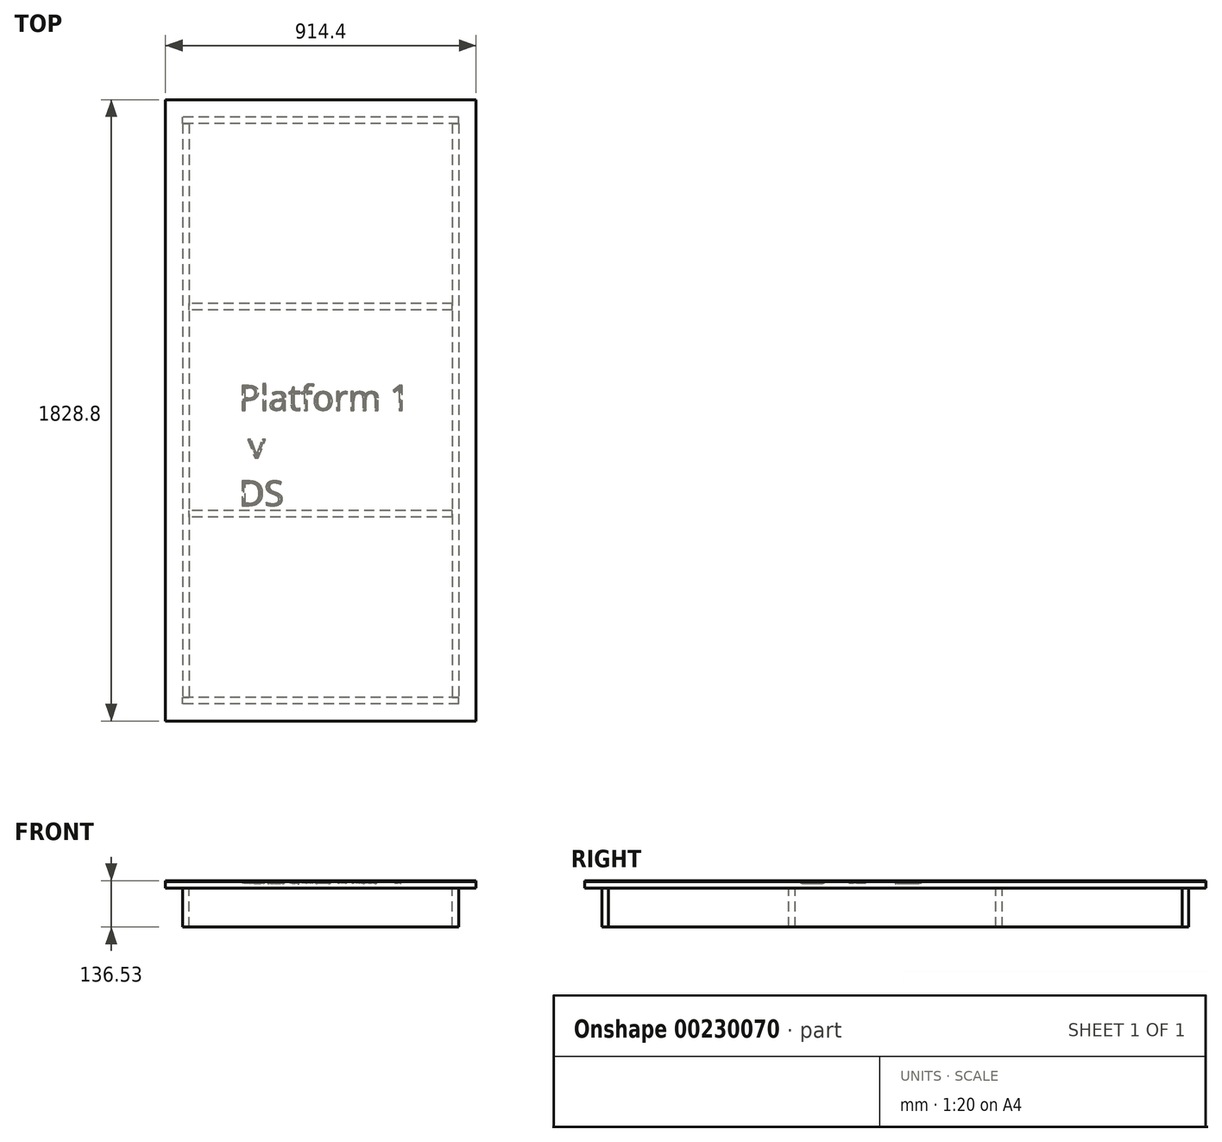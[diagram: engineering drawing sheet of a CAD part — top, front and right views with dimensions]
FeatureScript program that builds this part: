
annotation { "Feature Type Name" : "Feature", "Feature Type Description" : "" }
export const myFeature = defineFeature(function(context is Context, id is Id, definition is map)
    precondition{}
    {
        {
            var Q0;
            Q0=qCreatedBy(makeId("Top.planeOp"),FACE);
            var sketch = newSketch(context, id + "F0", { "sketchPlane" : qUnion([Q0])});
            skLineSegment(sketch, "E0.top", {"start": v(457.2, 914.4) * mm, "end": v(-457.2, 914.4) * mm});
            skLineSegment(sketch, "E0.right", {"start": v(-457.2, -914.4) * mm, "end": v(-457.2, 914.4) * mm});
            skPoint(sketch, "E0.middle", {"position": v(0, 0) * mm});
            skLineSegment(sketch, "E1.0", {"start": v(-406.4, -863.6) * mm, "end": v(-406.4, 863.6) * mm});
            skLineSegment(sketch, "E1.1", {"start": v(406.4, -863.6) * mm, "end": v(-406.4, -863.6) * mm});
            skLineSegment(sketch, "E1.2", {"start": v(406.4, -863.6) * mm, "end": v(406.4, 863.6) * mm});
            skLineSegment(sketch, "E1.3", {"start": v(406.4, 863.6) * mm, "end": v(-406.4, 863.6) * mm});
            skLineSegment(sketch, "E2.0", {"start": v(406.4, -844.55) * mm, "end": v(-406.4, -844.55) * mm});
            skLineSegment(sketch, "E3.0", {"start": v(406.4, 844.55) * mm, "end": v(-406.4, 844.55) * mm});
            skLineSegment(sketch, "E4.0", {"start": v(-387.35, -844.55) * mm, "end": v(-387.35, 844.55) * mm});
            skLineSegment(sketch, "E5.0", {"start": v(387.35, -844.55) * mm, "end": v(387.35, 844.55) * mm});
            skLineSegment(sketch, "E6.trimOffspring", {"start": v(387.35, -295.28) * mm, "end": v(-387.35, -295.28) * mm});
            skLineSegment(sketch, "E7.trimOffspring", {"start": v(387.35, -314.33) * mm, "end": v(-387.35, -314.33) * mm});
            skLineSegment(sketch, "E8.trimOffspring", {"start": v(387.35, 295.27) * mm, "end": v(-387.35, 295.27) * mm});
            skLineSegment(sketch, "E9.trimOffspring", {"start": v(387.35, 314.32) * mm, "end": v(-387.35, 314.32) * mm});
            skLineSegment(sketch, "E10", {"start": v(457.2, 914.4) * mm, "end": v(457.2, -914.4) * mm});
            skLineSegment(sketch, "E11", {"start": v(457.2, -914.4) * mm, "end": v(-457.2, -914.4) * mm});
            skLineSegment(sketch, "E12", {"start": v(0, 914.4) * mm, "end": v(0, -914.4) * mm, "construction": true});
            skSolve(sketch);
        }
        {
            var Q0;
            Q0 = qSketchRegion(id + "F0", true);
            var Q1;
            {var subQ0=sQuery(id+"F0.wireOp",EDGE,"E2.0");var subQ1=sQuery(id+"F0.wireOp",EDGE,"E1.0");var subQ2=makeQuery(id+"F0.imprint","INTERSECT",VERTEX,{"derivedFrom":[subQ1,subQ0]});Q1=makeQuery(id+"F0.imprint","IMPRINT",FACE,{"disambiguationData":[TD([[makeQuery(id+"F0.imprint","IMPRINT",EDGE,{"disambiguationData":[TD([[subQ2,-1.0]])],"derivedFrom":subQ1}),-1.0]])]});}
            var Q2;
            {var subQ0=sQuery(id+"F0.wireOp",EDGE,"E6.trimOffspring");Q2=makeQuery(id+"F0.imprint","IMPRINT",FACE,{"disambiguationData":[TD([[makeQuery(id+"F0.imprint","IMPRINT",EDGE,{"derivedFrom":subQ0}),-1.0]])]});}
            var Q3;
            {var subQ0=sQuery(id+"F0.wireOp",EDGE,"E8.trimOffspring");Q3=makeQuery(id+"F0.imprint","IMPRINT",FACE,{"disambiguationData":[TD([[makeQuery(id+"F0.imprint","IMPRINT",EDGE,{"derivedFrom":subQ0}),-1.0]])]});}
            var Q4;
            {var subQ5=sQuery(id+"F0.wireOp",EDGE,"E9.trimOffspring");Q4=makeQuery(id+"F0.imprint","IMPRINT",FACE,{"disambiguationData":[TD([[makeQuery(id+"F0.imprint","IMPRINT",EDGE,{"derivedFrom":subQ5}),-1.0]])]});}
            var Q5;
            {var subQ5=sQuery(id+"F0.wireOp",EDGE,"E7.trimOffspring");Q5=makeQuery(id+"F0.imprint","IMPRINT",FACE,{"disambiguationData":[TD([[makeQuery(id+"F0.imprint","IMPRINT",EDGE,{"derivedFrom":subQ5}),1.0]])]});}
            var Q6;
            {var subQ0=sQuery(id+"F0.wireOp",EDGE,"E6.trimOffspring");Q6=makeQuery(id+"F0.imprint","IMPRINT",FACE,{"disambiguationData":[TD([[makeQuery(id+"F0.imprint","IMPRINT",EDGE,{"derivedFrom":subQ0}),1.0]])]});}
            var Q7;
            {var subQ4=sQuery(id+"F0.wireOp",EDGE,"E1.2");var subQ11=sQuery(id+"F0.wireOp",EDGE,"E2.0");var subQ12=makeQuery(id+"F0.imprint","INTERSECT",VERTEX,{"derivedFrom":[subQ4,subQ11]});Q7=makeQuery(id+"F0.imprint","IMPRINT",FACE,{"disambiguationData":[TD([[makeQuery(id+"F0.imprint","IMPRINT",EDGE,{"disambiguationData":[TD([[subQ12,-1.0]])],"derivedFrom":subQ4}),1.0]])]});}
            var Q8;
            {var subQ0=sQuery(id+"F0.wireOp",EDGE,"E1.3");Q8=makeQuery(id+"F0.imprint","IMPRINT",FACE,{"disambiguationData":[TD([[makeQuery(id+"F0.imprint","IMPRINT",EDGE,{"derivedFrom":subQ0}),1.0]])]});}
            var Q9;
            {var subQ4=sQuery(id+"F0.wireOp",EDGE,"E1.1");Q9=makeQuery(id+"F0.imprint","IMPRINT",FACE,{"disambiguationData":[TD([[makeQuery(id+"F0.imprint","IMPRINT",EDGE,{"derivedFrom":subQ4}),-1.0]])]});}
            extrude(context, id + "F1", {"entities" : qUnion([Q0, Q1, Q2, Q3, Q4, Q5, Q6, Q7, Q8, Q9]), "depth" : 19.05 * mm});
        }
        {
            var Q0;
            Q0=makeQuery(id+"F1.opExtrude","CAP_FACE",FACE,{"disambiguationData":[OSD([sQuery(id+"F0.wireOp",EDGE,"E0.bottom"),sQuery(id+"F0.wireOp",EDGE,"E0.top"),sQuery(id+"F0.wireOp",EDGE,"E0.left"),sQuery(id+"F0.wireOp",EDGE,"E0.right")])],"isStart":false});
            extrude(context, id + "F2", {"entities" : qUnion([Q0]), "depth" : 3.17 * mm});
        }
        {
            var Q0;
            {var subQ4=sQuery(id+"F0.wireOp",EDGE,"E1.1");Q0=makeQuery(id+"F0.imprint","IMPRINT",FACE,{"disambiguationData":[TD([[makeQuery(id+"F0.imprint","IMPRINT",EDGE,{"derivedFrom":subQ4}),-1.0]])]});}
            var Q1;
            {var subQ0=sQuery(id+"F0.wireOp",EDGE,"E1.3");Q1=makeQuery(id+"F0.imprint","IMPRINT",FACE,{"disambiguationData":[TD([[makeQuery(id+"F0.imprint","IMPRINT",EDGE,{"derivedFrom":subQ0}),1.0]])]});}
            var Q2;
            {var subQ0=sQuery(id+"F0.wireOp",EDGE,"E8.trimOffspring");Q2=makeQuery(id+"F0.imprint","IMPRINT",FACE,{"disambiguationData":[TD([[makeQuery(id+"F0.imprint","IMPRINT",EDGE,{"derivedFrom":subQ0}),-1.0]])]});}
            var Q3;
            {var subQ0=sQuery(id+"F0.wireOp",EDGE,"E6.trimOffspring");Q3=makeQuery(id+"F0.imprint","IMPRINT",FACE,{"disambiguationData":[TD([[makeQuery(id+"F0.imprint","IMPRINT",EDGE,{"derivedFrom":subQ0}),1.0]])]});}
            extrude(context, id + "F3", {"entities" : qUnion([Q0, Q1, Q2, Q3]), "oppositeDirection" : true, "depth" : 114.3 * mm});
        }
        {
            var Q0;
            {var subQ1=sQuery(id+"F0.wireOp",EDGE,"E2.0");var subQ4=sQuery(id+"F0.wireOp",EDGE,"E1.2");var subQ5=makeQuery(id+"F0.imprint","INTERSECT",VERTEX,{"derivedFrom":[subQ4,subQ1]});Q0=makeQuery(id+"F0.imprint","IMPRINT",FACE,{"disambiguationData":[TD([[makeQuery(id+"F0.imprint","IMPRINT",EDGE,{"disambiguationData":[TD([[subQ5,-1.0]])],"derivedFrom":subQ4}),1.0]])]});}
            var Q1;
            {var subQ1=sQuery(id+"F0.wireOp",EDGE,"E2.0");var subQ4=sQuery(id+"F0.wireOp",EDGE,"E1.0");var subQ5=makeQuery(id+"F0.imprint","INTERSECT",VERTEX,{"derivedFrom":[subQ4,subQ1]});Q1=makeQuery(id+"F0.imprint","IMPRINT",FACE,{"disambiguationData":[TD([[makeQuery(id+"F0.imprint","IMPRINT",EDGE,{"disambiguationData":[TD([[subQ5,-1.0]])],"derivedFrom":subQ4}),-1.0]])]});}
            var Q2;
            Q2=makeQuery(id+"F3.opExtrude","CAP_FACE",FACE,{"disambiguationData":[OSD([sQuery(id+"F0.wireOp",EDGE,"E1.0"),sQuery(id+"F0.wireOp",EDGE,"E1.1"),sQuery(id+"F0.wireOp",EDGE,"E1.2"),sQuery(id+"F0.wireOp",EDGE,"E2.0")])],"isStart":false});
            extrude(context, id + "F4", {"entities" : qUnion([Q0, Q1]), "endBound" : BoundingType.UP_TO_SURFACE, "oppositeDirection" : true, "endBoundEntityFace" : qUnion([Q2]), "depth" : 25.4 * mm});
        }
        {
            var Q0;
            Q0=makeQuery(id+"F1.opExtrude","CAP_FACE",FACE,{"disambiguationData":[OSD([sQuery(id+"F0.wireOp",EDGE,"E0.bottom"),sQuery(id+"F0.wireOp",EDGE,"E0.top"),sQuery(id+"F0.wireOp",EDGE,"E0.left"),sQuery(id+"F0.wireOp",EDGE,"E0.right")])],"isStart":false});
            var sketch = newSketch(context, id + "F5", { "sketchPlane" : qUnion([Q0])});
            skText(sketch, "E13", { "text": "Platform 1\n v\nDS", "fontName": "OpenSans-Regular.ttf"});
            const initialGuessF5  = {"E13": [-0.24177, 0, 1, 0, 0.07437]};
            skSetInitialGuess(sketch, initialGuessF5);
            skSolve(sketch);
        }
        {
            var Q0;
            Q0 = qSketchRegion(id + "F5", true);
            extrude(context, id + "F6", {"entities" : qUnion([Q0]), "operationType" : NewBodyOperationType.REMOVE, "oppositeDirection" : true, "depth" : 6.35 * mm, "hasDraft" : true, "draftAngle" : 45 * degree, "draftPullDirection" : true});
        }
    });
